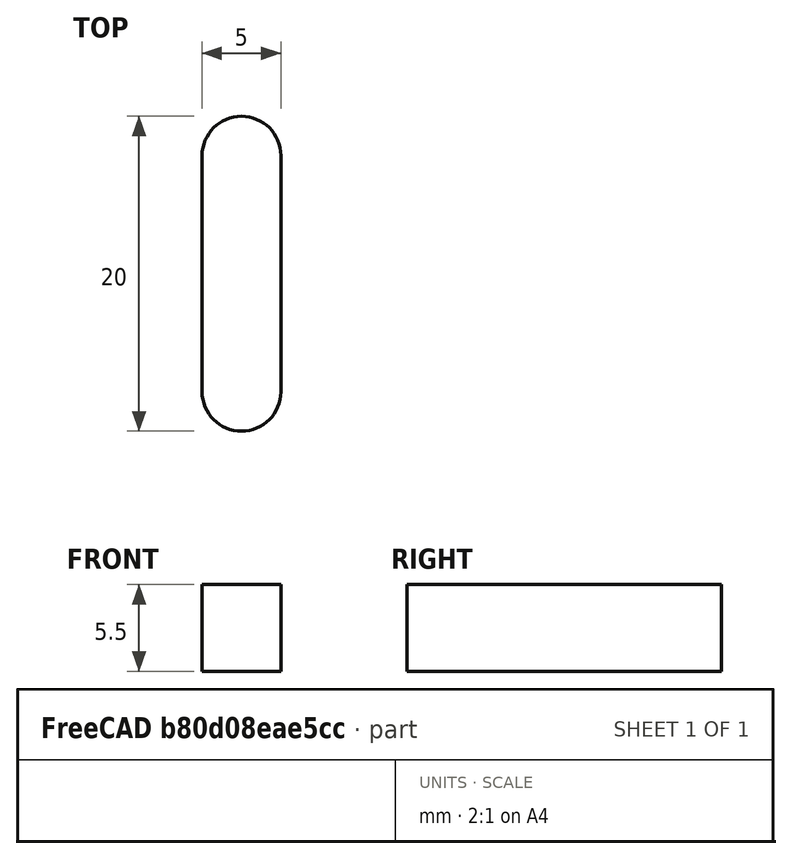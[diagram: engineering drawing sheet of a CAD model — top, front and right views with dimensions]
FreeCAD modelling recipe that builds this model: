
FCSTD DOCUMENT  (FreeCAD 0.20R29603 (Git))
Label: Key
License: All rights reserved
LicenseURL: http://en.wikipedia.org/wiki/All_rights_reserved
objects: Sketcher::SketchObject×1, Part::Extrusion×1
note: 2 computed .brp shape members not serialized (recipe doc carries the construction recipe); baked Part::Feature solids carry a one-line shape summary decoded from their .brp

FEATURE [Sketcher::SketchObject] Sketch
  FullyConstrained = true
  sketch-geometry (4):
    g0: ArcOfCircle CenterX=0 CenterY=0 CenterZ=0 NormalX=0 NormalY=0 NormalZ=1 AngleXU=0 Radius=2.5 StartAngle=3.14159 EndAngle=6.28319
    g1: ArcOfCircle CenterX=0 CenterY=15 CenterZ=0 NormalX=0 NormalY=0 NormalZ=1 AngleXU=0 Radius=2.5 StartAngle=-2.141e-13 EndAngle=3.14159
    g2: LineSegment StartX=2.5 StartY=-2.16519e-11 StartZ=0 EndX=2.5 EndY=15 EndZ=0
    g3: LineSegment StartX=-2.5 StartY=15 StartZ=0 EndX=-2.5 EndY=-2.1652e-11 EndZ=0
  constraints (9):
    c: Tangent(g0,g2) = -1.5708
    c: Tangent(g2,g1) = -1.5708
    c: Tangent(g1,g3) = -1.5708
    c: Tangent(g3,g0) = -1.5708
    c: Equal(g0,g1)
    c: Coincident(g0,g-1)
    c: Distance(g1,g0) = 15
    c: Distance(g1,g1) = 5
    c: Vertical(g0,g1)
FEATURE [Part::Extrusion] Extrude
  Base = -> Sketch
  Dir = (0,0,1)
  DirMode = 2
  FaceMakerClass = Part::FaceMakerBullseye
  LengthFwd = 5.5
  LengthRev = 0
  Solid = true
  Symmetric = false
